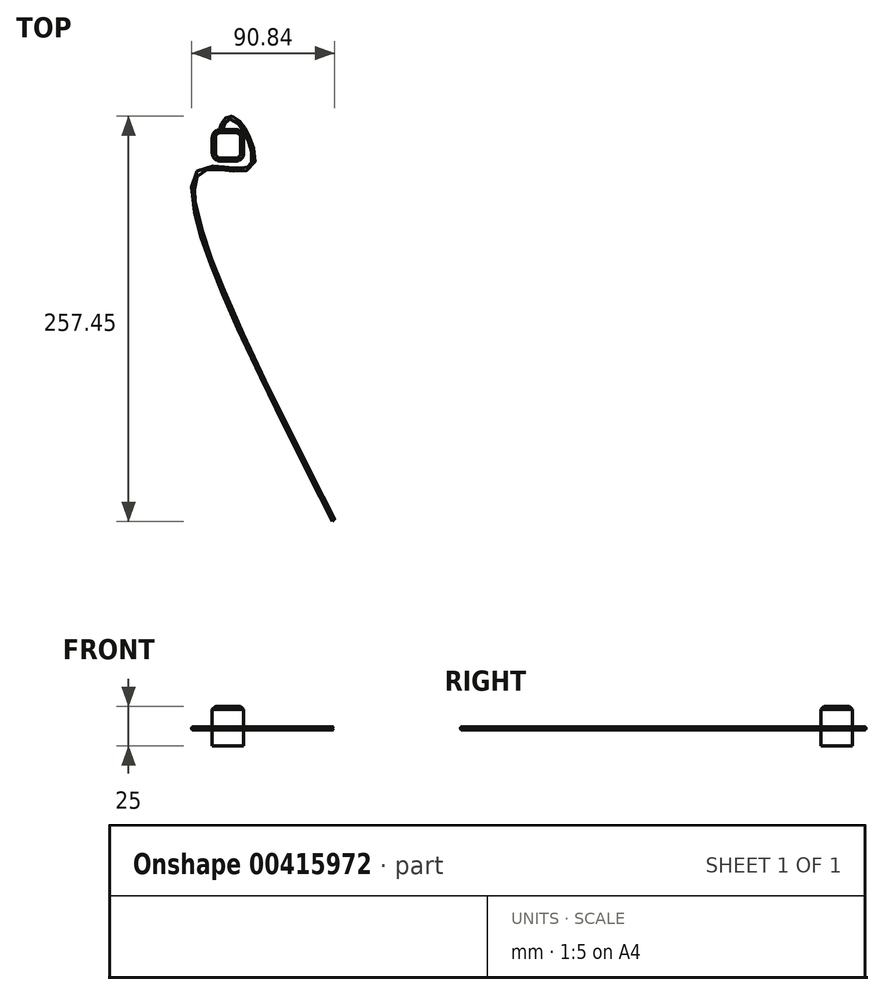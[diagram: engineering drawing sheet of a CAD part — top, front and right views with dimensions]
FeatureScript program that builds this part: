
annotation { "Feature Type Name" : "Feature", "Feature Type Description" : "" }
export const myFeature = defineFeature(function(context is Context, id is Id, definition is map)
    precondition{}
    {
        {
            var Q0;
            Q0=qCreatedBy(makeId("Top.planeOp"),FACE);
            var sketch = newSketch(context, id + "F0", { "sketchPlane" : qUnion([Q0])});
            skLineSegment(sketch, "E0.bottom", {"start": v(5, -10) * mm, "end": v(-5, -10) * mm});
            skLineSegment(sketch, "E0.top", {"start": v(5, 10) * mm, "end": v(-5, 10) * mm});
            skLineSegment(sketch, "E0.left", {"start": v(10, -5) * mm, "end": v(10, 5) * mm});
            skLineSegment(sketch, "E0.right", {"start": v(-10, -5) * mm, "end": v(-10, 5) * mm});
            skPoint(sketch, "E0.middle", {"position": v(0, 0) * mm});
            skPoint(sketch, "E1.visualSharp", {"position": v(10, 10) * mm});
            skArc(sketch, "E1.filletArc", {"start": v(10, 5) * mm, "mid": v(8.54, 8.54) * mm, "end": v(5, 10) * mm});
            skPoint(sketch, "E2.visualSharp", {"position": v(-10, 10) * mm});
            skArc(sketch, "E2.filletArc", {"start": v(-5, 10) * mm, "mid": v(-8.54, 8.54) * mm, "end": v(-10, 5) * mm});
            skPoint(sketch, "E3.visualSharp", {"position": v(-10, -10) * mm});
            skArc(sketch, "E3.filletArc", {"start": v(-10, -5) * mm, "mid": v(-8.54, -8.54) * mm, "end": v(-5, -10) * mm});
            skPoint(sketch, "E4.visualSharp", {"position": v(10, -10) * mm});
            skArc(sketch, "E4.filletArc", {"start": v(5, -10) * mm, "mid": v(8.54, -8.54) * mm, "end": v(10, -5) * mm});
            skSolve(sketch);
        }
        {
            var Q0;
            Q0 = qSketchRegion(id + "F0", true);
            var Q1;
            Q1=sQuery(id+"F0.wireOp",EDGE,"E0.bottom");
            var Q2;
            Q2=sQuery(id+"F0.wireOp",EDGE,"E4.filletArc");
            var Q3;
            Q3=sQuery(id+"F0.wireOp",EDGE,"E0.left");
            var Q4;
            Q4=sQuery(id+"F0.wireOp",EDGE,"E1.filletArc");
            var Q5;
            Q5=sQuery(id+"F0.wireOp",EDGE,"E0.top");
            var Q6;
            Q6=sQuery(id+"F0.wireOp",EDGE,"E2.filletArc");
            var Q7;
            Q7=sQuery(id+"F0.wireOp",EDGE,"E0.right");
            var Q8;
            Q8=sQuery(id+"F0.wireOp",EDGE,"E3.filletArc");
            extrude(context, id + "F1", {"entities" : qUnion([Q0]), "surfaceEntities" : qUnion([Q1, Q2, Q3, Q4, Q5, Q6, Q7, Q8]), "depth" : 25 * mm});
        }
        {
            var Q0;
            Q0=makeQuery(id+"F1.opExtrude","CAP_EDGE",EDGE,{"disambiguationData":[OSD([sQuery(id+"F0.wireOp",EDGE,"E1.filletArc")])],"isStart":false});
            var Q1;
            Q1=makeQuery(id+"F1.opExtrude","CAP_EDGE",EDGE,{"disambiguationData":[OSD([sQuery(id+"F0.wireOp",EDGE,"E2.filletArc")])],"isStart":false});
            var Q2;
            Q2=makeQuery(id+"F1.opExtrude","CAP_EDGE",EDGE,{"disambiguationData":[OSD([sQuery(id+"F0.wireOp",EDGE,"E4.filletArc")])],"isStart":false});
            var Q3;
            Q3=makeQuery(id+"F1.opExtrude","CAP_EDGE",EDGE,{"disambiguationData":[OSD([sQuery(id+"F0.wireOp",EDGE,"E3.filletArc")])],"isStart":false});
            var Q4;
            Q4=makeQuery(id+"F1.opExtrude","CAP_EDGE",EDGE,{"disambiguationData":[OSD([sQuery(id+"F0.wireOp",EDGE,"E0.left")])],"isStart":false});
            var Q5;
            Q5=makeQuery(id+"F1.opExtrude","CAP_EDGE",EDGE,{"disambiguationData":[OSD([sQuery(id+"F0.wireOp",EDGE,"E0.right")])],"isStart":false});
            var Q6;
            Q6=makeQuery(id+"F1.opExtrude","CAP_EDGE",EDGE,{"disambiguationData":[OSD([sQuery(id+"F0.wireOp",EDGE,"E0.top")])],"isStart":false});
            var Q7;
            Q7=makeQuery(id+"F1.opExtrude","CAP_EDGE",EDGE,{"disambiguationData":[OSD([sQuery(id+"F0.wireOp",EDGE,"E0.bottom")])],"isStart":false});
            chamfer(context, id + "F2", {"entities" : qUnion([Q0, Q1, Q2, Q3, Q4, Q5, Q6, Q7]), "width" : 2 * mm, "tangentPropagation" : true});
        }
        {
            var Q0;
            Q0=makeQuery(id+"F1.opExtrude","CAP_FACE",FACE,{"disambiguationData":[OSD([sQuery(id+"F0.wireOp",EDGE,"E0.bottom"),sQuery(id+"F0.wireOp",EDGE,"E0.top"),sQuery(id+"F0.wireOp",EDGE,"E0.left"),sQuery(id+"F0.wireOp",EDGE,"E0.right"),sQuery(id+"F0.wireOp",EDGE,"E1.filletArc"),sQuery(id+"F0.wireOp",EDGE,"E2.filletArc"),sQuery(id+"F0.wireOp",EDGE,"E3.filletArc"),sQuery(id+"F0.wireOp",EDGE,"E4.filletArc")])],"isStart":false});
            var sketch = newSketch(context, id + "F3", { "sketchPlane" : qUnion([Q0])});
            skFitSpline(sketch, "E5", {"points": [v(0, 0) * mm, v(-5, 5) * mm, v(2.18, 17.6) * mm, v(15.22, -12.73) * mm, v(-16.62, -15.46) * mm, v(67.02, -238.11) * mm], "startDerivative": vector(-85.65, 35.82) * mm, "endDerivative": vector(346.41, -683.1) * mm});
            skSolve(sketch);
        }
        {
            var Q0;
            Q0=qCreatedBy(makeId("Right.planeOp"),FACE);
            var sketch = newSketch(context, id + "F4", { "sketchPlane" : qUnion([Q0])});
            skCircle(sketch, "E6", {"center": v(0, 11.06) * mm, "radius": 1 * mm});
            skSolve(sketch);
        }
        {
            var Q0;
            Q0 = qSketchRegion(id + "F4", true);
            var Q1;
            Q1 = qBodyType(qCreatedBy(id + "F3" ,EDGE), BodyType.WIRE);
            sweep(context, id + "F5", {"operationType" : NewBodyOperationType.ADD, "profiles" : qUnion([Q0]), "path" : qUnion([Q1])});
        }
    });
